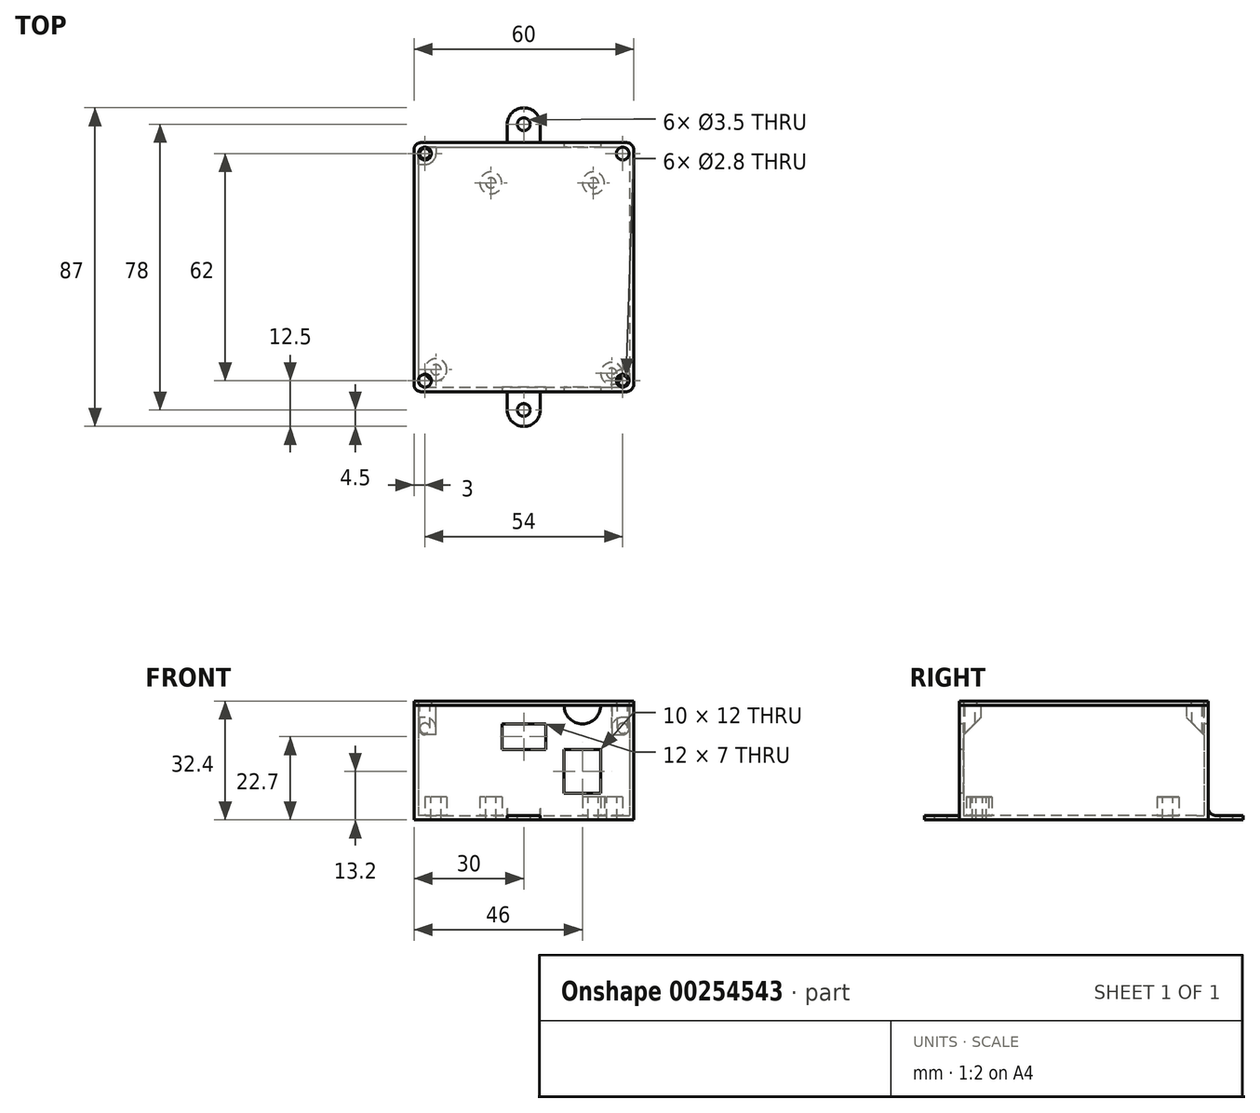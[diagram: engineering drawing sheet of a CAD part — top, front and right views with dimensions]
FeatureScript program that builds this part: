
annotation { "Feature Type Name" : "Feature", "Feature Type Description" : "" }
export const myFeature = defineFeature(function(context is Context, id is Id, definition is map)
    precondition{}
    {
        {
            var Q0;
            Q0=qCreatedBy(makeId("Top.planeOp"),FACE);
            var sketch = newSketch(context, id + "F0", { "sketchPlane" : qUnion([Q0])});
            skLineSegment(sketch, "E0.bottom", {"start": v(0, 0) * mm, "end": v(60, 0) * mm});
            skLineSegment(sketch, "E0.top", {"start": v(0, -68) * mm, "end": v(60, -68) * mm});
            skLineSegment(sketch, "E0.left", {"start": v(0, 0) * mm, "end": v(0, -68) * mm});
            skLineSegment(sketch, "E0.right", {"start": v(60, 0) * mm, "end": v(60, -68) * mm});
            skCircle(sketch, "E1", {"center": v(6, -62) * mm, "radius": 1.4 * mm});
            skCircle(sketch, "E2", {"center": v(54, -63) * mm, "radius": 1.4 * mm});
            skCircle(sketch, "E3", {"center": v(21, -11) * mm, "radius": 1.4 * mm});
            skCircle(sketch, "E4", {"center": v(49, -11) * mm, "radius": 1.4 * mm});
            skLineSegment(sketch, "E5", {"start": v(6, -62) * mm, "end": v(54, -62) * mm, "construction": true});
            skLineSegment(sketch, "E6", {"start": v(54, -62) * mm, "end": v(54, -63) * mm, "construction": true});
            skLineSegment(sketch, "E7", {"start": v(54, -62) * mm, "end": v(54, -11) * mm, "construction": true});
            skLineSegment(sketch, "E8", {"start": v(54, -11) * mm, "end": v(49, -11) * mm, "construction": true});
            skLineSegment(sketch, "E9", {"start": v(49, -11) * mm, "end": v(21, -11) * mm, "construction": true});
            skCircle(sketch, "E10", {"center": v(21, -11) * mm, "radius": 3 * mm});
            skCircle(sketch, "E11", {"center": v(49, -11) * mm, "radius": 3 * mm});
            skCircle(sketch, "E12", {"center": v(6, -62) * mm, "radius": 3 * mm});
            skCircle(sketch, "E13", {"center": v(54, -63) * mm, "radius": 3 * mm});
            skLineSegment(sketch, "E14.bottom", {"start": v(1.2, -1.2) * mm, "end": v(58.8, -1.2) * mm});
            skLineSegment(sketch, "E14.top", {"start": v(1.2, -66.8) * mm, "end": v(58.8, -66.8) * mm});
            skLineSegment(sketch, "E14.left", {"start": v(1.2, -1.2) * mm, "end": v(1.2, -66.8) * mm});
            skLineSegment(sketch, "E14.right", {"start": v(58.8, -1.2) * mm, "end": v(58.8, -66.8) * mm});
            skLineSegment(sketch, "E15", {"start": v(0, -34) * mm, "end": v(1.2, -34) * mm, "construction": true});
            skLineSegment(sketch, "E16", {"start": v(30, 0) * mm, "end": v(30, -1.2) * mm, "construction": true});
            skLineSegment(sketch, "E17", {"start": v(25.5, -68) * mm, "end": v(25.5, -73) * mm});
            skLineSegment(sketch, "E18", {"start": v(34.5, -68) * mm, "end": v(34.5, -73) * mm});
            skLineSegment(sketch, "E19", {"start": v(34.5, -73) * mm, "end": v(25.5, -73) * mm, "construction": true});
            skArc(sketch, "E20", {"start": v(25.5, -73) * mm, "mid": v(30, -77.5) * mm, "end": v(34.5, -73) * mm});
            skCircle(sketch, "E21", {"center": v(30, -73) * mm, "radius": 1.75 * mm});
            skLineSegment(sketch, "E22", {"start": v(30, -68) * mm, "end": v(30, -73) * mm, "construction": true});
            skLineSegment(sketch, "E23.MirrorCS", {"start": v(25.5, 0) * mm, "end": v(25.5, 5) * mm});
            skArc(sketch, "E24.MirrorCS", {"start": v(25.5, 5) * mm, "mid": v(30, 9.5) * mm, "end": v(34.5, 5) * mm});
            skLineSegment(sketch, "E25.MirrorCS", {"start": v(34.5, 0) * mm, "end": v(34.5, 5) * mm});
            skLineSegment(sketch, "E26.MirrorCS", {"start": v(30, 0) * mm, "end": v(30, 5) * mm, "construction": true});
            skCircle(sketch, "E27.MirrorC", {"center": v(30, 5) * mm, "radius": 1.75 * mm});
            skSolve(sketch);
        }
        {
            var Q0;
            {var subQ1=sQuery(id+"F0.wireOp",EDGE,"E0.left");Q0=makeQuery(id+"F0.imprint","IMPRINT",FACE,{"disambiguationData":[TD([[makeQuery(id+"F0.imprint","IMPRINT",EDGE,{"derivedFrom":subQ1}),1.0]])]});}
            var Q1;
            Q1=makeQuery(id+"F0.imprint","IMPRINT",FACE,{"disambiguationData":[TD([[makeQuery(id+"F0.imprint","IMPRINT",EDGE,{"derivedFrom":sQuery(id+"F0.wireOp",EDGE,"E10")}),-1.0]])]});
            var Q2;
            {var subQ1=sQuery(id+"F0.wireOp",EDGE,"E23.MirrorCS");Q2=makeQuery(id+"F0.imprint","IMPRINT",FACE,{"disambiguationData":[TD([[makeQuery(id+"F0.imprint","IMPRINT",EDGE,{"derivedFrom":subQ1}),-1.0]])]});}
            var Q3;
            {var subQ1=sQuery(id+"F0.wireOp",EDGE,"E17");Q3=makeQuery(id+"F0.imprint","IMPRINT",FACE,{"disambiguationData":[TD([[makeQuery(id+"F0.imprint","IMPRINT",EDGE,{"derivedFrom":subQ1}),1.0]])]});}
            var Q4;
            Q4=makeQuery(id+"F0.imprint","IMPRINT",FACE,{"disambiguationData":[TD([[makeQuery(id+"F0.imprint","IMPRINT",EDGE,{"derivedFrom":sQuery(id+"F0.wireOp",EDGE,"E1")}),-1.0]])]});
            var Q5;
            Q5=makeQuery(id+"F0.imprint","IMPRINT",FACE,{"disambiguationData":[TD([[makeQuery(id+"F0.imprint","IMPRINT",EDGE,{"derivedFrom":sQuery(id+"F0.wireOp",EDGE,"E2")}),-1.0]])]});
            var Q6;
            Q6=makeQuery(id+"F0.imprint","IMPRINT",FACE,{"disambiguationData":[TD([[makeQuery(id+"F0.imprint","IMPRINT",EDGE,{"derivedFrom":sQuery(id+"F0.wireOp",EDGE,"E4")}),-1.0]])]});
            var Q7;
            Q7=makeQuery(id+"F0.imprint","IMPRINT",FACE,{"disambiguationData":[TD([[makeQuery(id+"F0.imprint","IMPRINT",EDGE,{"derivedFrom":sQuery(id+"F0.wireOp",EDGE,"E3")}),-1.0]])]});
            extrude(context, id + "F1", {"entities" : qUnion([Q0, Q1, Q2, Q3, Q4, Q5, Q6, Q7]), "oppositeDirection" : true, "depth" : 1.2 * mm});
        }
        {
            var Q0;
            {var subQ1=sQuery(id+"F0.wireOp",EDGE,"E0.left");Q0=makeQuery(id+"F0.imprint","IMPRINT",FACE,{"disambiguationData":[TD([[makeQuery(id+"F0.imprint","IMPRINT",EDGE,{"derivedFrom":subQ1}),1.0]])]});}
            extrude(context, id + "F2", {"entities" : qUnion([Q0]), "operationType" : NewBodyOperationType.ADD, "depth" : 30 * mm});
        }
        {
            var Q0;
            Q0=makeQuery(id+"F0.imprint","IMPRINT",FACE,{"disambiguationData":[TD([[makeQuery(id+"F0.imprint","IMPRINT",EDGE,{"derivedFrom":sQuery(id+"F0.wireOp",EDGE,"E1")}),-1.0]])]});
            var Q1;
            Q1=makeQuery(id+"F0.imprint","IMPRINT",FACE,{"disambiguationData":[TD([[makeQuery(id+"F0.imprint","IMPRINT",EDGE,{"derivedFrom":sQuery(id+"F0.wireOp",EDGE,"E2")}),-1.0]])]});
            var Q2;
            Q2=makeQuery(id+"F0.imprint","IMPRINT",FACE,{"disambiguationData":[TD([[makeQuery(id+"F0.imprint","IMPRINT",EDGE,{"derivedFrom":sQuery(id+"F0.wireOp",EDGE,"E4")}),-1.0]])]});
            var Q3;
            Q3=makeQuery(id+"F0.imprint","IMPRINT",FACE,{"disambiguationData":[TD([[makeQuery(id+"F0.imprint","IMPRINT",EDGE,{"derivedFrom":sQuery(id+"F0.wireOp",EDGE,"E3")}),-1.0]])]});
            extrude(context, id + "F3", {"entities" : qUnion([Q0, Q1, Q2, Q3]), "operationType" : NewBodyOperationType.ADD, "depth" : 5 * mm});
        }
        {
            var Q0;
            {var subQ0=sQuery(id+"F0.wireOp",EDGE,"E0.top");Q0=makeQuery(id+"F2.boolean.opBoolean","MERGE",FACE,{"derivedFrom":[makeQuery(id+"F1.opExtrude","SWEPT_FACE",FACE,{"disambiguationData":[OSD([subQ0]),TDD([makeQuery(id+"F0.imprint","IMPRINT",EDGE,{"disambiguationData":[TD([[makeQuery(id+"F0.imprint","INTERSECT",VERTEX,{"derivedFrom":[subQ0,sQuery(id+"F0.wireOp",EDGE,"E0.left")]}),-1.0]])],"derivedFrom":subQ0})])]}),makeQuery(id+"F1.opExtrude","SWEPT_FACE",FACE,{"disambiguationData":[OSD([subQ0]),TDD([makeQuery(id+"F0.imprint","IMPRINT",EDGE,{"disambiguationData":[TD([[makeQuery(id+"F0.imprint","INTERSECT",VERTEX,{"derivedFrom":[subQ0,sQuery(id+"F0.wireOp",EDGE,"E0.right")]}),1.0]])],"derivedFrom":subQ0})])]}),makeQuery(id+"F2.opExtrude","SWEPT_FACE",FACE,{"disambiguationData":[OSD([subQ0])]})]});}
            var sketch = newSketch(context, id + "F4", { "sketchPlane" : qUnion([Q0])});
            skLineSegment(sketch, "E28.bottom", {"start": v(41, 18) * mm, "end": v(51, 18) * mm});
            skLineSegment(sketch, "E28.top", {"start": v(41, 6) * mm, "end": v(51, 6) * mm});
            skLineSegment(sketch, "E28.left", {"start": v(41, 18) * mm, "end": v(41, 6) * mm});
            skLineSegment(sketch, "E28.right", {"start": v(51, 18) * mm, "end": v(51, 6) * mm});
            skLineSegment(sketch, "E29.bottom", {"start": v(24, 25) * mm, "end": v(36, 25) * mm});
            skLineSegment(sketch, "E29.top", {"start": v(24, 18) * mm, "end": v(36, 18) * mm});
            skLineSegment(sketch, "E29.left", {"start": v(24, 25) * mm, "end": v(24, 18) * mm});
            skLineSegment(sketch, "E29.right", {"start": v(36, 25) * mm, "end": v(36, 18) * mm});
            skArc(sketch, "E30", {"start": v(41, 30) * mm, "mid": v(46, 25) * mm, "end": v(51, 30) * mm});
            skLineSegment(sketch, "E31", {"start": v(51, 18) * mm, "end": v(51, 30) * mm, "construction": true});
            skLineSegment(sketch, "E32", {"start": v(41, 18) * mm, "end": v(41, 30) * mm, "construction": true});
            skSolve(sketch);
        }
        {
            var Q0;
            Q0=makeQuery(id+"F4.imprint","IMPRINT",FACE,{"disambiguationData":[TD([[makeQuery(id+"F4.imprint","IMPRINT",EDGE,{"derivedFrom":sQuery(id+"F4.wireOp",EDGE,"E29.bottom")}),-1.0]])]});
            var Q1;
            Q1=makeQuery(id+"F4.imprint","IMPRINT",FACE,{"disambiguationData":[TD([[makeQuery(id+"F4.imprint","IMPRINT",EDGE,{"derivedFrom":sQuery(id+"F4.wireOp",EDGE,"E28.bottom")}),-1.0]])]});
            extrude(context, id + "F5", {"entities" : qUnion([Q0, Q1]), "operationType" : NewBodyOperationType.REMOVE, "oppositeDirection" : true, "depth" : 25 * mm});
        }
        {
            var Q0;
            {var subQ0=sQuery(id+"F4.wireOp",EDGE,"E30");Q0=makeQuery(id+"F4.imprint","IMPRINT",FACE,{"disambiguationData":[TD([[makeQuery(id+"F4.imprint","IMPRINT",EDGE,{"derivedFrom":subQ0}),1.0]])]});}
            extrude(context, id + "F6", {"entities" : qUnion([Q0]), "operationType" : NewBodyOperationType.REMOVE, "endBound" : BoundingType.THROUGH_ALL, "oppositeDirection" : true, "depth" : 25 * mm});
        }
        {
            var Q0;
            Q0=makeQuery(id+"F2.opExtrude","CAP_EDGE",EDGE,{"disambiguationData":[OSD([sQuery(id+"F0.wireOp",EDGE,"E0.top")])],"isStart":true});
            var Q1;
            Q1=makeQuery(id+"F2.opExtrude","CAP_EDGE",EDGE,{"disambiguationData":[OSD([sQuery(id+"F0.wireOp",EDGE,"E0.bottom")])],"isStart":true});
            fillet(context, id + "F7", {"entities" : qUnion([Q0, Q1]), "radius" : 2 * mm, "tangentPropagation" : true, "allowEdgeOverflow" : false});
        }
        {
            var Q0;
            {var subQ0=sQuery(id+"F0.wireOp",EDGE,"E14.bottom");var subQ1=sQuery(id+"F0.wireOp",EDGE,"E0.left");var subQ2=sQuery(id+"F0.wireOp",EDGE,"E0.top");var subQ3=sQuery(id+"F0.wireOp",EDGE,"E0.bottom");var subQ4=sQuery(id+"F0.wireOp",EDGE,"E14.left");var subQ5=sQuery(id+"F0.wireOp",EDGE,"E14.top");var subQ6=sQuery(id+"F0.wireOp",EDGE,"E0.right");Q0=makeQuery(id+"F6.boolean.opBoolean","SPLIT",FACE,{"disambiguationData":[TD([makeQuery(id+"F1.opExtrude","SWEPT_FACE",FACE,{"disambiguationData":[OSD([subQ1])]})])],"derivedFrom":makeQuery(id+"F2.opExtrude","CAP_FACE",FACE,{"disambiguationData":[OSD([subQ3,subQ2,subQ1,subQ6,subQ0,subQ5,subQ4,sQuery(id+"F0.wireOp",EDGE,"E14.right")])],"isStart":false})});}
            var sketch = newSketch(context, id + "F8", { "sketchPlane" : qUnion([Q0])});
            skLineSegment(sketch, "E33", {"start": v(0, -6) * mm, "end": v(6, 0) * mm, "construction": true});
            skCircle(sketch, "E34", {"center": v(3, -3) * mm, "radius": 1.4 * mm});
            skLineSegment(sketch, "E35.bottom", {"start": v(0, 0) * mm, "end": v(6, 0) * mm});
            skLineSegment(sketch, "E35.top", {"start": v(0, -6) * mm, "end": v(3, -6) * mm});
            skLineSegment(sketch, "E35.left", {"start": v(0, 0) * mm, "end": v(0, -6) * mm});
            skLineSegment(sketch, "E35.right", {"start": v(6, 0) * mm, "end": v(6, -3) * mm});
            skPoint(sketch, "E36.visualSharp", {"position": v(6, -6) * mm});
            skArc(sketch, "E36.filletArc", {"start": v(3, -6) * mm, "mid": v(5.12, -5.12) * mm, "end": v(6, -3) * mm});
            skArc(sketch, "E37.MirrorCS", {"start": v(57, -6) * mm, "mid": v(54.88, -5.12) * mm, "end": v(54, -3) * mm});
            skLineSegment(sketch, "E38.MirrorCS", {"start": v(54, 0) * mm, "end": v(54, -3) * mm});
            skLineSegment(sketch, "E39.MirrorCS", {"start": v(60, 0) * mm, "end": v(54, 0) * mm});
            skLineSegment(sketch, "E40.MirrorCS", {"start": v(60, 0) * mm, "end": v(60, -6) * mm});
            skLineSegment(sketch, "E41.MirrorCS", {"start": v(60, -6) * mm, "end": v(57, -6) * mm});
            skCircle(sketch, "E42.MirrorC", {"center": v(57, -3) * mm, "radius": 1.4 * mm});
            skLineSegment(sketch, "E43.MirrorCS", {"start": v(0, -62) * mm, "end": v(3, -62) * mm});
            skArc(sketch, "E44.MirrorCS", {"start": v(3, -62) * mm, "mid": v(5.12, -62.88) * mm, "end": v(6, -65) * mm});
            skLineSegment(sketch, "E45.MirrorCS", {"start": v(6, -68) * mm, "end": v(6, -65) * mm});
            skLineSegment(sketch, "E46.MirrorCS", {"start": v(0, -68) * mm, "end": v(6, -68) * mm});
            skLineSegment(sketch, "E47.MirrorCS", {"start": v(0, -68) * mm, "end": v(0, -62) * mm});
            skCircle(sketch, "E48.MirrorC", {"center": v(3, -65) * mm, "radius": 1.4 * mm});
            skLineSegment(sketch, "E49.MirrorCS", {"start": v(60, -68) * mm, "end": v(60, -62) * mm});
            skLineSegment(sketch, "E50.MirrorCS", {"start": v(60, -68) * mm, "end": v(54, -68) * mm});
            skLineSegment(sketch, "E51.MirrorCS", {"start": v(54, -68) * mm, "end": v(54, -65) * mm});
            skArc(sketch, "E52.MirrorCS", {"start": v(57, -62) * mm, "mid": v(54.88, -62.88) * mm, "end": v(54, -65) * mm});
            skLineSegment(sketch, "E53.MirrorCS", {"start": v(60, -62) * mm, "end": v(57, -62) * mm});
            skCircle(sketch, "E54.MirrorC", {"center": v(57, -65) * mm, "radius": 1.4 * mm});
            skSolve(sketch);
        }
        {
            var Q0;
            {var subQ7=sQuery(id+"F8.wireOp",EDGE,"E35.bottom");Q0=makeQuery(id+"F8.imprint","IMPRINT",FACE,{"disambiguationData":[TD([[makeQuery(id+"F8.imprint","IMPRINT",EDGE,{"derivedFrom":subQ7}),-1.0]])]});}
            var Q1;
            Q1=makeQuery(id+"F8.imprint","IMPRINT",FACE,{"disambiguationData":[TD([[makeQuery(id+"F8.imprint","IMPRINT",EDGE,{"derivedFrom":sQuery(id+"F8.wireOp",EDGE,"E34")}),-1.0]])]});
            var Q2;
            Q2=makeQuery(id+"F8.imprint","IMPRINT",FACE,{"disambiguationData":[TD([[makeQuery(id+"F8.imprint","IMPRINT",EDGE,{"derivedFrom":sQuery(id+"F8.wireOp",EDGE,"E37.MirrorCS")}),-1.0]])]});
            var Q3;
            Q3=makeQuery(id+"F8.imprint","IMPRINT",FACE,{"disambiguationData":[TD([[makeQuery(id+"F8.imprint","IMPRINT",EDGE,{"derivedFrom":sQuery(id+"F8.wireOp",EDGE,"E49.MirrorCS")}),1.0]])]});
            var Q4;
            {var subQ0=sQuery(id+"F8.wireOp",EDGE,"E46.MirrorCS");Q4=makeQuery(id+"F8.imprint","IMPRINT",FACE,{"disambiguationData":[TD([[makeQuery(id+"F8.imprint","IMPRINT",EDGE,{"derivedFrom":subQ0}),1.0]])]});}
            var Q5;
            {var subQ1=sQuery(id+"F8.wireOp",EDGE,"E44.MirrorCS");Q5=makeQuery(id+"F8.imprint","IMPRINT",FACE,{"disambiguationData":[TD([[makeQuery(id+"F8.imprint","IMPRINT",EDGE,{"derivedFrom":subQ1}),-1.0]])]});}
            extrude(context, id + "F9", {"entities" : qUnion([Q0, Q1, Q2, Q3, Q4, Q5]), "operationType" : NewBodyOperationType.ADD, "oppositeDirection" : true, "depth" : 3 * mm});
        }
        {
            var Q0;
            Q0=makeQuery(id+"F9.boolean.opBoolean","INTERSECT",EDGE,{"derivedFrom":[makeQuery(id+"F2.opExtrude","SWEPT_FACE",FACE,{"disambiguationData":[OSD([sQuery(id+"F0.wireOp",EDGE,"E14.bottom")])]}),makeQuery(id+"F9.opExtrude","CAP_FACE",FACE,{"disambiguationData":[OSD([sQuery(id+"F8.wireOp",EDGE,"E34"),sQuery(id+"F8.wireOp",EDGE,"E35.bottom"),sQuery(id+"F8.wireOp",EDGE,"E35.top"),sQuery(id+"F8.wireOp",EDGE,"E35.left"),sQuery(id+"F8.wireOp",EDGE,"E35.right"),sQuery(id+"F8.wireOp",EDGE,"E36.filletArc")])],"isStart":false})]});
            var Q1;
            Q1=makeQuery(id+"F9.boolean.opBoolean","INTERSECT",EDGE,{"derivedFrom":[makeQuery(id+"F2.opExtrude","SWEPT_FACE",FACE,{"disambiguationData":[OSD([sQuery(id+"F0.wireOp",EDGE,"E14.bottom")])]}),makeQuery(id+"F9.opExtrude","CAP_FACE",FACE,{"disambiguationData":[OSD([sQuery(id+"F8.wireOp",EDGE,"E37.MirrorCS"),sQuery(id+"F8.wireOp",EDGE,"E38.MirrorCS"),sQuery(id+"F8.wireOp",EDGE,"E39.MirrorCS"),sQuery(id+"F8.wireOp",EDGE,"E40.MirrorCS"),sQuery(id+"F8.wireOp",EDGE,"E41.MirrorCS"),sQuery(id+"F8.wireOp",EDGE,"E42.MirrorC")])],"isStart":false})]});
            var Q2;
            Q2=makeQuery(id+"F9.boolean.opBoolean","INTERSECT",EDGE,{"derivedFrom":[makeQuery(id+"F2.opExtrude","SWEPT_FACE",FACE,{"disambiguationData":[OSD([sQuery(id+"F0.wireOp",EDGE,"E14.top")])]}),makeQuery(id+"F9.opExtrude","CAP_FACE",FACE,{"disambiguationData":[OSD([sQuery(id+"F8.wireOp",EDGE,"E49.MirrorCS"),sQuery(id+"F8.wireOp",EDGE,"E50.MirrorCS"),sQuery(id+"F8.wireOp",EDGE,"E51.MirrorCS"),sQuery(id+"F8.wireOp",EDGE,"E52.MirrorCS"),sQuery(id+"F8.wireOp",EDGE,"E53.MirrorCS"),sQuery(id+"F8.wireOp",EDGE,"E54.MirrorC")])],"isStart":false})]});
            var Q3;
            Q3=makeQuery(id+"F9.boolean.opBoolean","INTERSECT",EDGE,{"derivedFrom":[makeQuery(id+"F2.opExtrude","SWEPT_FACE",FACE,{"disambiguationData":[OSD([sQuery(id+"F0.wireOp",EDGE,"E14.top")])]}),makeQuery(id+"F9.opExtrude","CAP_FACE",FACE,{"disambiguationData":[OSD([sQuery(id+"F8.wireOp",EDGE,"E43.MirrorCS"),sQuery(id+"F8.wireOp",EDGE,"E44.MirrorCS"),sQuery(id+"F8.wireOp",EDGE,"E45.MirrorCS"),sQuery(id+"F8.wireOp",EDGE,"E46.MirrorCS"),sQuery(id+"F8.wireOp",EDGE,"E47.MirrorCS"),sQuery(id+"F8.wireOp",EDGE,"E48.MirrorC")])],"isStart":false})]});
            chamfer(context, id + "F10", {"entities" : qUnion([Q0, Q1, Q2, Q3]), "width" : 5 * mm, "tangentPropagation" : true});
        }
        {
            var Q0;
            {var subQ0=sQuery(id+"F0.wireOp",EDGE,"E14.bottom");var subQ1=sQuery(id+"F0.wireOp",EDGE,"E0.left");var subQ2=sQuery(id+"F0.wireOp",EDGE,"E0.top");var subQ3=sQuery(id+"F0.wireOp",EDGE,"E0.bottom");var subQ4=sQuery(id+"F0.wireOp",EDGE,"E14.left");var subQ5=sQuery(id+"F0.wireOp",EDGE,"E14.top");var subQ6=sQuery(id+"F0.wireOp",EDGE,"E0.right");Q0=makeQuery(id+"F9.boolean.opBoolean","MERGE",FACE,{"derivedFrom":[makeQuery(id+"F6.boolean.opBoolean","SPLIT",FACE,{"disambiguationData":[TD([makeQuery(id+"F1.opExtrude","SWEPT_FACE",FACE,{"disambiguationData":[OSD([subQ1])]})])],"derivedFrom":makeQuery(id+"F2.opExtrude","CAP_FACE",FACE,{"disambiguationData":[OSD([subQ3,subQ2,subQ1,subQ6,subQ0,subQ5,subQ4,sQuery(id+"F0.wireOp",EDGE,"E14.right")])],"isStart":false})}),makeQuery(id+"F9.opExtrude","CAP_FACE",FACE,{"disambiguationData":[OSD([sQuery(id+"F8.wireOp",EDGE,"E34"),sQuery(id+"F8.wireOp",EDGE,"E35.bottom"),sQuery(id+"F8.wireOp",EDGE,"E35.top"),sQuery(id+"F8.wireOp",EDGE,"E35.left"),sQuery(id+"F8.wireOp",EDGE,"E35.right"),sQuery(id+"F8.wireOp",EDGE,"E36.filletArc")])],"isStart":true}),makeQuery(id+"F9.opExtrude","CAP_FACE",FACE,{"disambiguationData":[OSD([sQuery(id+"F8.wireOp",EDGE,"E43.MirrorCS"),sQuery(id+"F8.wireOp",EDGE,"E44.MirrorCS"),sQuery(id+"F8.wireOp",EDGE,"E45.MirrorCS"),sQuery(id+"F8.wireOp",EDGE,"E46.MirrorCS"),sQuery(id+"F8.wireOp",EDGE,"E47.MirrorCS"),sQuery(id+"F8.wireOp",EDGE,"E48.MirrorC")])],"isStart":true})]});}
            var sketch = newSketch(context, id + "F11", { "sketchPlane" : qUnion([Q0])});
            skLineSegment(sketch, "E55.bottom", {"start": v(0, 0) * mm, "end": v(60, 0) * mm});
            skLineSegment(sketch, "E55.top", {"start": v(0, -68) * mm, "end": v(60, -68) * mm});
            skLineSegment(sketch, "E55.left", {"start": v(0, 0) * mm, "end": v(0, -68) * mm});
            skLineSegment(sketch, "E55.right", {"start": v(60, 0) * mm, "end": v(60, -68) * mm});
            skCircle(sketch, "E56", {"center": v(3, -3) * mm, "radius": 1.75 * mm});
            skCircle(sketch, "E57", {"center": v(57, -3) * mm, "radius": 1.75 * mm});
            skCircle(sketch, "E58", {"center": v(57, -65) * mm, "radius": 1.75 * mm});
            skCircle(sketch, "E59", {"center": v(3, -65) * mm, "radius": 1.75 * mm});
            skLineSegment(sketch, "E60", {"start": v(3, -3) * mm, "end": v(57, -3) * mm, "construction": true});
            skLineSegment(sketch, "E61", {"start": v(57, -65) * mm, "end": v(3, -65) * mm, "construction": true});
            skLineSegment(sketch, "E62", {"start": v(57, -65) * mm, "end": v(57, -3) * mm, "construction": true});
            skLineSegment(sketch, "E63", {"start": v(30, -3) * mm, "end": v(30, 0) * mm, "construction": true});
            skLineSegment(sketch, "E64", {"start": v(3, -3) * mm, "end": v(3, -65) * mm, "construction": true});
            skLineSegment(sketch, "E65", {"start": v(57, -34) * mm, "end": v(60, -34) * mm, "construction": true});
            skSolve(sketch);
        }
        {
            var Q0;
            Q0 = qSketchRegion(id + "F11", true);
            extrude(context, id + "F12", {"entities" : qUnion([Q0]), "depth" : 1.2 * mm});
        }
        {
            var Q0;
            {var subQ0=sQuery(id+"F0.wireOp",EDGE,"E0.right");var subQ1=sQuery(id+"F0.wireOp",EDGE,"E0.top");Q0=makeQuery(id+"F2.boolean.opBoolean","MERGE",EDGE,{"derivedFrom":[makeQuery(id+"F1.opExtrude","SWEPT_EDGE",EDGE,{"disambiguationData":[OSD([subQ1,subQ0])]}),makeQuery(id+"F2.opExtrude","SWEPT_EDGE",EDGE,{"disambiguationData":[OSD([subQ1,subQ0])]})]});}
            var Q1;
            {var subQ0=sQuery(id+"F0.wireOp",EDGE,"E0.right");var subQ1=sQuery(id+"F0.wireOp",EDGE,"E0.bottom");Q1=makeQuery(id+"F2.boolean.opBoolean","MERGE",EDGE,{"derivedFrom":[makeQuery(id+"F1.opExtrude","SWEPT_EDGE",EDGE,{"disambiguationData":[OSD([subQ1,subQ0])]}),makeQuery(id+"F2.opExtrude","SWEPT_EDGE",EDGE,{"disambiguationData":[OSD([subQ1,subQ0])]})]});}
            var Q2;
            {var subQ0=sQuery(id+"F0.wireOp",EDGE,"E0.left");var subQ1=sQuery(id+"F0.wireOp",EDGE,"E0.top");Q2=makeQuery(id+"F2.boolean.opBoolean","MERGE",EDGE,{"derivedFrom":[makeQuery(id+"F1.opExtrude","SWEPT_EDGE",EDGE,{"disambiguationData":[OSD([subQ1,subQ0])]}),makeQuery(id+"F2.opExtrude","SWEPT_EDGE",EDGE,{"disambiguationData":[OSD([subQ1,subQ0])]})]});}
            var Q3;
            {var subQ0=sQuery(id+"F0.wireOp",EDGE,"E0.left");var subQ1=sQuery(id+"F0.wireOp",EDGE,"E0.bottom");Q3=makeQuery(id+"F2.boolean.opBoolean","MERGE",EDGE,{"derivedFrom":[makeQuery(id+"F1.opExtrude","SWEPT_EDGE",EDGE,{"disambiguationData":[OSD([subQ1,subQ0])]}),makeQuery(id+"F2.opExtrude","SWEPT_EDGE",EDGE,{"disambiguationData":[OSD([subQ1,subQ0])]})]});}
            fillet(context, id + "F13", {"entities" : qUnion([Q0, Q1, Q2, Q3]), "radius" : 2 * mm, "tangentPropagation" : true, "allowEdgeOverflow" : false});
        }
        {
            var Q0;
            Q0=makeQuery(id+"F2.opExtrude","SWEPT_EDGE",EDGE,{"disambiguationData":[OSD([sQuery(id+"F0.wireOp",EDGE,"E14.bottom"),sQuery(id+"F0.wireOp",EDGE,"E14.right")])]});
            var Q1;
            Q1=makeQuery(id+"F2.opExtrude","SWEPT_EDGE",EDGE,{"disambiguationData":[OSD([sQuery(id+"F0.wireOp",EDGE,"E14.bottom"),sQuery(id+"F0.wireOp",EDGE,"E14.left")])]});
            var Q2;
            Q2=makeQuery(id+"F2.opExtrude","SWEPT_EDGE",EDGE,{"disambiguationData":[OSD([sQuery(id+"F0.wireOp",EDGE,"E14.top"),sQuery(id+"F0.wireOp",EDGE,"E14.left")])]});
            var Q3;
            Q3=makeQuery(id+"F2.opExtrude","SWEPT_EDGE",EDGE,{"disambiguationData":[OSD([sQuery(id+"F0.wireOp",EDGE,"E14.top"),sQuery(id+"F0.wireOp",EDGE,"E14.right")])]});
            fillet(context, id + "F14", {"entities" : qUnion([Q0, Q1, Q2, Q3]), "radius" : 2 * mm, "tangentPropagation" : true, "allowEdgeOverflow" : false});
        }
        {
            var Q0;
            Q0=makeQuery(id+"F12.opExtrude","SWEPT_EDGE",EDGE,{"disambiguationData":[OSD([sQuery(id+"F11.wireOp",EDGE,"E55.top"),sQuery(id+"F11.wireOp",EDGE,"E55.left")])]});
            var Q1;
            Q1=makeQuery(id+"F12.opExtrude","SWEPT_EDGE",EDGE,{"disambiguationData":[OSD([sQuery(id+"F11.wireOp",EDGE,"E55.bottom"),sQuery(id+"F11.wireOp",EDGE,"E55.left")])]});
            var Q2;
            Q2=makeQuery(id+"F12.opExtrude","SWEPT_EDGE",EDGE,{"disambiguationData":[OSD([sQuery(id+"F11.wireOp",EDGE,"E55.top"),sQuery(id+"F11.wireOp",EDGE,"E55.right")])]});
            var Q3;
            Q3=makeQuery(id+"F12.opExtrude","SWEPT_EDGE",EDGE,{"disambiguationData":[OSD([sQuery(id+"F11.wireOp",EDGE,"E55.bottom"),sQuery(id+"F11.wireOp",EDGE,"E55.right")])]});
            fillet(context, id + "F15", {"entities" : qUnion([Q0, Q1, Q2, Q3]), "radius" : 2 * mm, "tangentPropagation" : true, "allowEdgeOverflow" : false});
        }
    });
